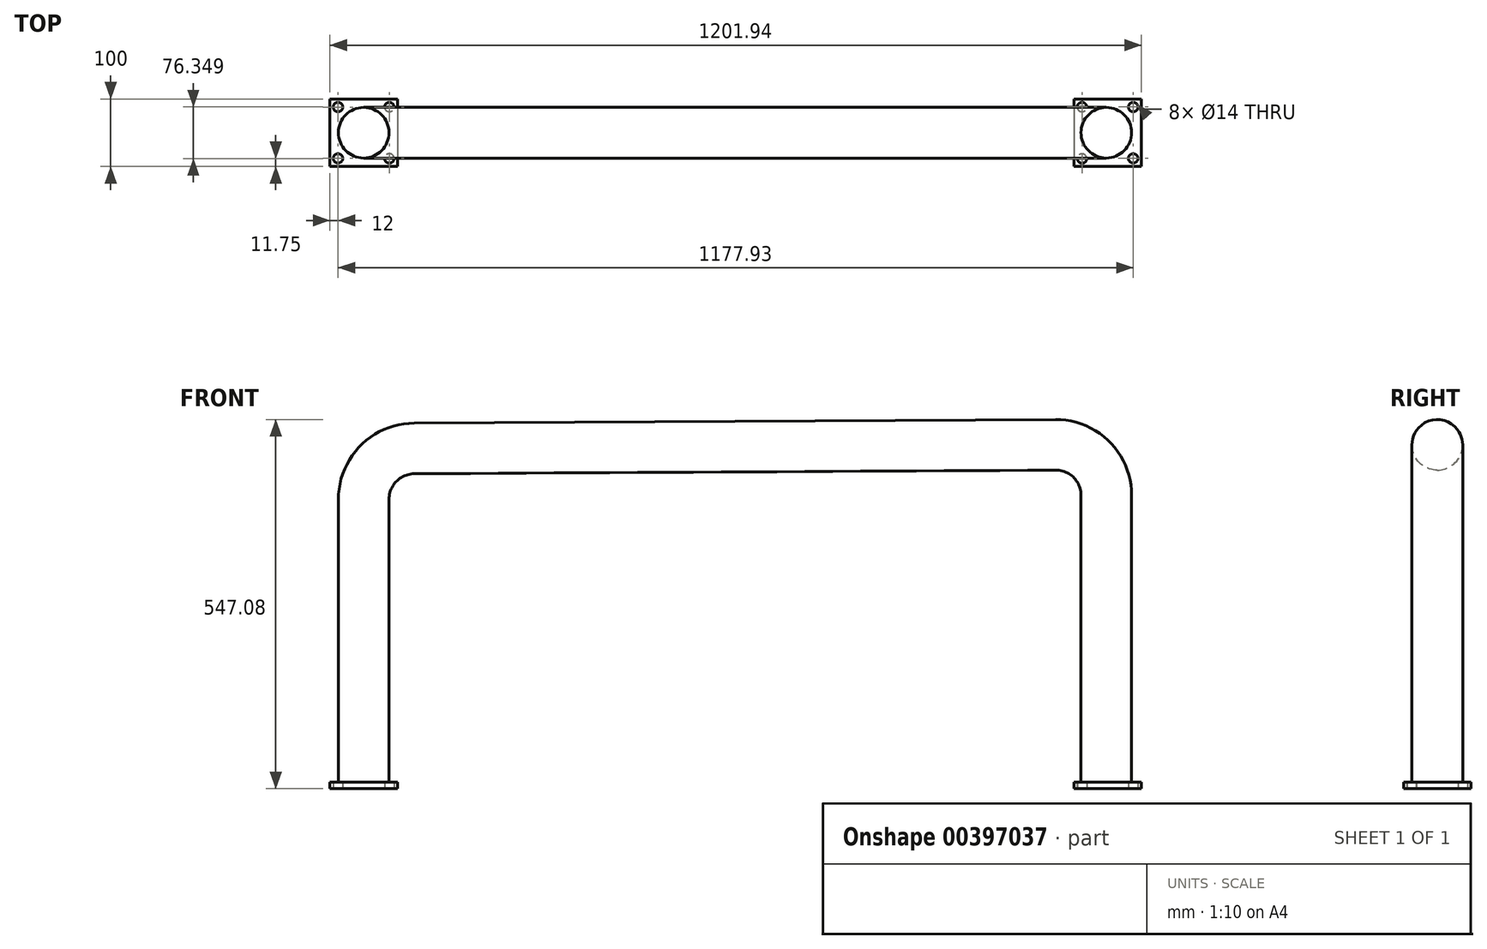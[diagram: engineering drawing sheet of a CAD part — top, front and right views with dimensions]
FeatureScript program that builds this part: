
annotation { "Feature Type Name" : "Feature", "Feature Type Description" : "" }
export const myFeature = defineFeature(function(context is Context, id is Id, definition is map)
    precondition{}
    {
        {
            var Q0;
            Q0=qCreatedBy(makeId("Top.planeOp"),FACE);
            var sketch = newSketch(context, id + "F0", { "sketchPlane" : qUnion([Q0])});
            skCircle(sketch, "E0", {"center": v(0, 0) * mm, "radius": 37.5 * mm});
            skSolve(sketch);
        }
        {
            var Q0;
            Q0=qCreatedBy(makeId("Front.planeOp"),FACE);
            var sketch = newSketch(context, id + "F1", { "sketchPlane" : qUnion([Q0])});
            skArc(sketch, "E1", {"start": v(75, 494.22) * mm, "mid": v(21.94, 471.98) * mm, "end": v(0, 418.8) * mm});
            skArc(sketch, "E2", {"start": v(1100, 425) * mm, "mid": v(1078, 477.88) * mm, "end": v(1025, 499.58) * mm});
            skLineSegment(sketch, "E3", {"start": v(75, 494.22) * mm, "end": v(1025, 499.58) * mm});
            skLineSegment(sketch, "E4", {"start": v(1100, 425) * mm, "end": v(1100, 0) * mm});
            skLineSegment(sketch, "E5", {"start": v(0, 0) * mm, "end": v(0, 418.8) * mm});
            skSolve(sketch);
        }
        {
            var Q0;
            Q0=makeQuery(id+"F0.imprint","IMPRINT",FACE,{"disambiguationData":[TD([[makeQuery(id+"F0.imprint","IMPRINT",EDGE,{"derivedFrom":sQuery(id+"F0.wireOp",EDGE,"E0")}),1.0]])]});
            var Q1;
            Q1=sQuery(id+"F1.wireOp",EDGE,"E5");
            var Q2;
            Q2=sQuery(id+"F1.wireOp",EDGE,"E1");
            var Q3;
            Q3=sQuery(id+"F1.wireOp",EDGE,"E3");
            var Q4;
            Q4=sQuery(id+"F1.wireOp",EDGE,"E2");
            var Q5;
            Q5=sQuery(id+"F1.wireOp",EDGE,"E4");
            sweep(context, id + "F2", {"profiles" : qUnion([Q0]), "path" : qUnion([Q1, Q2, Q3, Q4, Q5])});
        }
        {
            var Q0;
            Q0=makeQuery(id+"F2.opSweep","CAP_FACE",FACE,{"disambiguationData":[OSD([sQuery(id+"F0.wireOp",EDGE,"E0"),sQuery(id+"F1.wireOp",VERTEX,"E5.start")])],"isStart":true});
            var sketch = newSketch(context, id + "F3", { "sketchPlane" : qUnion([Q0])});
            skLineSegment(sketch, "E6.bottom", {"start": v(-50, -50) * mm, "end": v(50, -50) * mm});
            skLineSegment(sketch, "E6.top", {"start": v(-50, 50) * mm, "end": v(50, 50) * mm});
            skLineSegment(sketch, "E6.left", {"start": v(-50, -50) * mm, "end": v(-50, 50) * mm});
            skLineSegment(sketch, "E6.right", {"start": v(50, -50) * mm, "end": v(50, 50) * mm});
            skPoint(sketch, "E6.middle", {"position": v(0, 0) * mm});
            skLineSegment(sketch, "E7.bottom", {"start": v(1051.94, -50) * mm, "end": v(1151.94, -50) * mm});
            skLineSegment(sketch, "E7.top", {"start": v(1051.94, 50) * mm, "end": v(1151.94, 50) * mm});
            skLineSegment(sketch, "E7.left", {"start": v(1051.94, -50) * mm, "end": v(1051.94, 50) * mm});
            skLineSegment(sketch, "E7.right", {"start": v(1151.94, -50) * mm, "end": v(1151.94, 50) * mm});
            skPoint(sketch, "E7.middle", {"position": v(1101.94, 0) * mm});
            skSolve(sketch);
        }
        {
            var Q0;
            Q0 = qSketchRegion(id + "F3", true);
            extrude(context, id + "F4", {"entities" : qUnion([Q0]), "operationType" : NewBodyOperationType.ADD, "depth" : 10 * mm});
        }
        {
            var Q0;
            Q0=makeQuery(id+"F4.opExtrude","CAP_FACE",FACE,{"disambiguationData":[OSD([sQuery(id+"F3.wireOp",EDGE,"E6.bottom"),sQuery(id+"F3.wireOp",EDGE,"E6.top"),sQuery(id+"F3.wireOp",EDGE,"E6.left"),sQuery(id+"F3.wireOp",EDGE,"E6.right")])],"isStart":false});
            var sketch = newSketch(context, id + "F5", { "sketchPlane" : qUnion([Q0])});
            skLineSegment(sketch, "E8", {"start": v(-50, 50) * mm, "end": v(-38, 50) * mm});
            skLineSegment(sketch, "E9", {"start": v(-38, 50) * mm, "end": v(-38, 38) * mm});
            skLineSegment(sketch, "E10", {"start": v(-50, -50) * mm, "end": v(-38, -50) * mm});
            skLineSegment(sketch, "E11", {"start": v(-38, -50) * mm, "end": v(-38, -38) * mm});
            skLineSegment(sketch, "E12", {"start": v(50, -50) * mm, "end": v(38, -50) * mm});
            skLineSegment(sketch, "E13", {"start": v(38, -50) * mm, "end": v(38, -38) * mm});
            skLineSegment(sketch, "E14", {"start": v(50, 50) * mm, "end": v(38, 50) * mm});
            skLineSegment(sketch, "E15", {"start": v(38, 50) * mm, "end": v(38, 38) * mm});
            skLineSegment(sketch, "E16", {"start": v(1052.08, 50.25) * mm, "end": v(1064.08, 50.25) * mm});
            skLineSegment(sketch, "E17", {"start": v(1064.08, 50.25) * mm, "end": v(1064.08, 38.25) * mm});
            skLineSegment(sketch, "E18", {"start": v(1151.87, 50.01) * mm, "end": v(1139.87, 50.01) * mm});
            skLineSegment(sketch, "E19", {"start": v(1139.87, 50.01) * mm, "end": v(1139.87, 38.01) * mm});
            skLineSegment(sketch, "E20", {"start": v(1151.93, -50.1) * mm, "end": v(1139.93, -50.1) * mm});
            skLineSegment(sketch, "E21", {"start": v(1139.93, -50.1) * mm, "end": v(1139.93, -38.1) * mm});
            skLineSegment(sketch, "E22", {"start": v(1051.99, -50.1) * mm, "end": v(1063.99, -50.1) * mm});
            skLineSegment(sketch, "E23", {"start": v(1063.99, -50.1) * mm, "end": v(1063.99, -38.1) * mm});
            skSolve(sketch);
        }
        {
            var Q0;
            Q0=sQuery(id+"F5.wireOp",VERTEX,"E9.end");
            var Q1;
            Q1=sQuery(id+"F5.wireOp",VERTEX,"E15.end");
            var Q2;
            Q2=sQuery(id+"F5.wireOp",VERTEX,"E13.end");
            var Q3;
            Q3=sQuery(id+"F5.wireOp",VERTEX,"E11.end");
            var Q4;
            Q4=sQuery(id+"F5.wireOp",VERTEX,"E17.end");
            var Q5;
            Q5=sQuery(id+"F5.wireOp",VERTEX,"E19.end");
            var Q6;
            Q6=sQuery(id+"F5.wireOp",VERTEX,"E21.end");
            var Q7;
            Q7=sQuery(id+"F5.wireOp",VERTEX,"E23.end");
            var Q8;
            Q8=makeQuery(id+"F2.opSweep","SWEPT_BODY",BODY,{"disambiguationData":[OSD([sQuery(id+"F0.wireOp",EDGE,"E0"),sQuery(id+"F1.wireOp",EDGE,"E4")])]});
            hole(context, id + "F6", {"style" : HoleStyle.SIMPLE, "endStyle" : HoleEndStyle.BLIND, "holeDiameter" : 14 * mm, "holeDepth" : 150 * mm, "isTappedThrough" : true, "tappedDepth" : 12 * mm, "tapClearance" : 3, "locations" : qUnion([Q0, Q1, Q2, Q3, Q4, Q5, Q6, Q7]), "scope" : qUnion([Q8])});
        }
    });
